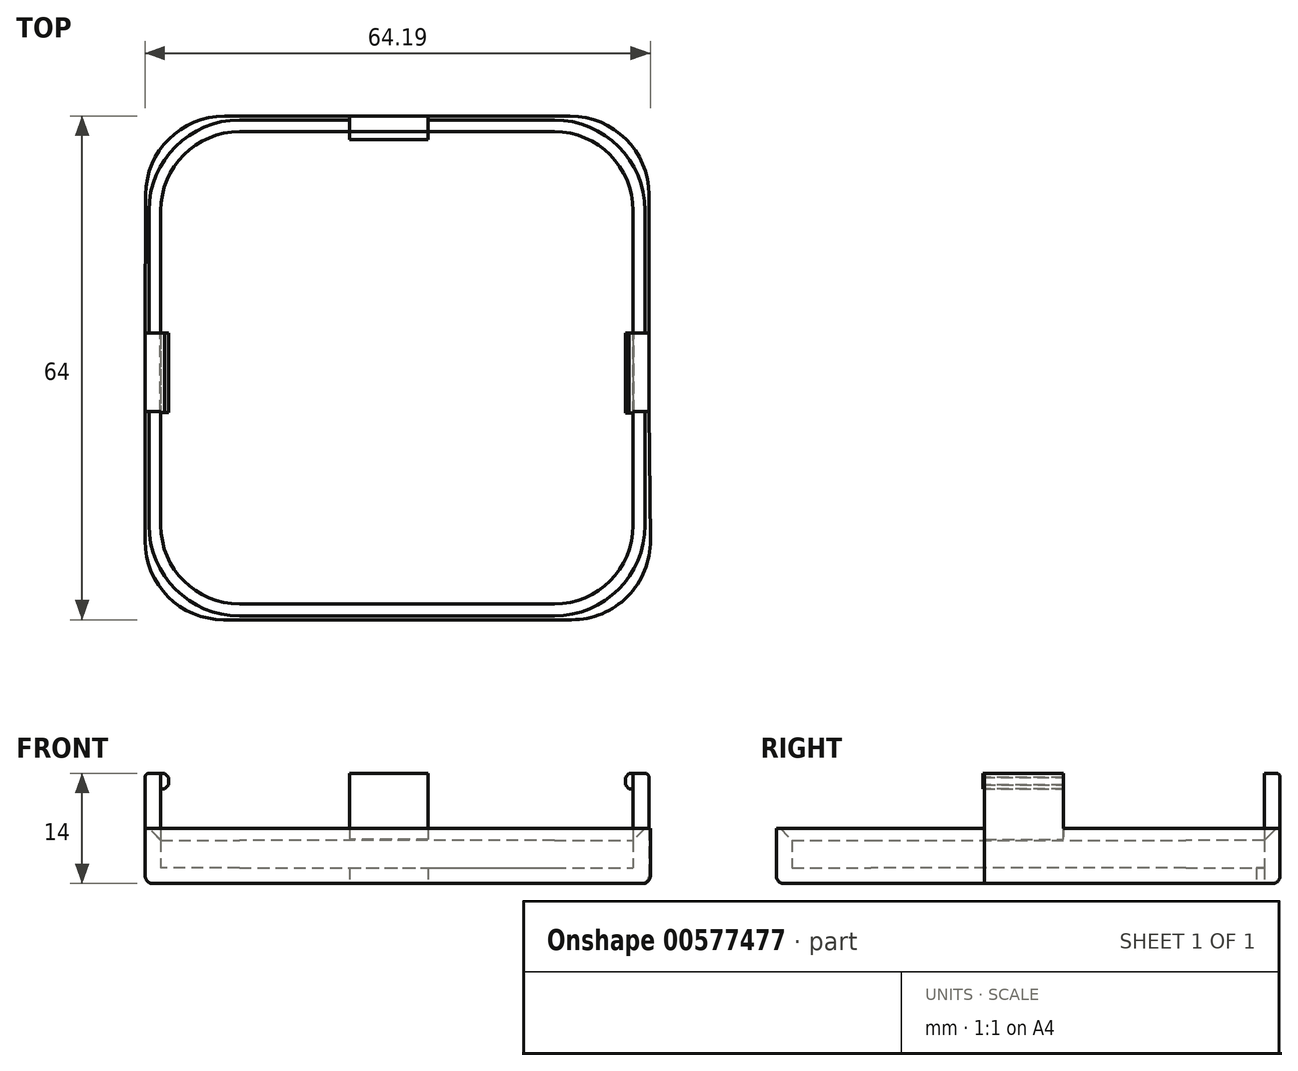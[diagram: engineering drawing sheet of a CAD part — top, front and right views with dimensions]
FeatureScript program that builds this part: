
annotation { "Feature Type Name" : "Feature", "Feature Type Description" : "" }
export const myFeature = defineFeature(function(context is Context, id is Id, definition is map)
    precondition{}
    {
        {
            var Q0;
            Q0=qCreatedBy(makeId("Top.planeOp"),FACE);
            var sketch = newSketch(context, id + "F0", { "sketchPlane" : qUnion([Q0])});
            skLineSegment(sketch, "E0.bottom", {"start": v(-28.96, 30.55) * mm, "end": v(31.04, 30.55) * mm});
            skLineSegment(sketch, "E0.top", {"start": v(-28.96, -29.45) * mm, "end": v(31.04, -29.45) * mm});
            skLineSegment(sketch, "E0.left", {"start": v(-28.96, 30.55) * mm, "end": v(-28.96, -29.45) * mm});
            skLineSegment(sketch, "E0.right", {"start": v(31.04, 30.55) * mm, "end": v(31.04, -29.45) * mm});
            skLineSegment(sketch, "E1.bottom", {"start": v(-5, 30.55) * mm, "end": v(5, 30.55) * mm});
            skLineSegment(sketch, "E1.top", {"start": v(-5, 32.55) * mm, "end": v(5, 32.55) * mm});
            skLineSegment(sketch, "E1.left", {"start": v(-5, 30.55) * mm, "end": v(-5, 32.55) * mm});
            skLineSegment(sketch, "E1.right", {"start": v(5, 30.55) * mm, "end": v(5, 32.55) * mm});
            skLineSegment(sketch, "E2.top", {"start": v(-5, 29.55) * mm, "end": v(5, 29.55) * mm});
            skLineSegment(sketch, "E2.left", {"start": v(-5, 30.55) * mm, "end": v(-5, 29.55) * mm});
            skLineSegment(sketch, "E2.right", {"start": v(5, 30.55) * mm, "end": v(5, 29.55) * mm});
            skLineSegment(sketch, "E3.bottom", {"start": v(31.04, 5) * mm, "end": v(33.04, 5) * mm});
            skLineSegment(sketch, "E3.top", {"start": v(31.04, -5) * mm, "end": v(33.04, -5) * mm});
            skLineSegment(sketch, "E3.left", {"start": v(31.04, 5) * mm, "end": v(31.04, -5) * mm});
            skLineSegment(sketch, "E3.right", {"start": v(33.04, 5) * mm, "end": v(33.04, -5) * mm});
            skLineSegment(sketch, "E4.bottom", {"start": v(31.04, 5) * mm, "end": v(30.04, 5) * mm});
            skLineSegment(sketch, "E4.top", {"start": v(31.04, -5.2) * mm, "end": v(30.04, -5.2) * mm});
            skLineSegment(sketch, "E4.left", {"start": v(31.04, 5) * mm, "end": v(31.04, -5.2) * mm});
            skLineSegment(sketch, "E4.right", {"start": v(30.04, 5) * mm, "end": v(30.04, -5.2) * mm});
            skLineSegment(sketch, "E5.bottom", {"start": v(-28.96, 5) * mm, "end": v(-30.96, 5) * mm});
            skLineSegment(sketch, "E5.top", {"start": v(-28.96, -5) * mm, "end": v(-30.96, -5) * mm});
            skLineSegment(sketch, "E5.left", {"start": v(-28.96, 5) * mm, "end": v(-28.96, -5) * mm});
            skLineSegment(sketch, "E5.right", {"start": v(-30.96, 5) * mm, "end": v(-30.96, -5) * mm});
            skLineSegment(sketch, "E6.bottom", {"start": v(-28.96, 5) * mm, "end": v(-27.96, 5) * mm});
            skLineSegment(sketch, "E6.top", {"start": v(-28.96, -5.13) * mm, "end": v(-27.96, -5.13) * mm});
            skLineSegment(sketch, "E6.left", {"start": v(-28.96, 5) * mm, "end": v(-28.96, -5.13) * mm});
            skLineSegment(sketch, "E6.right", {"start": v(-27.96, 5) * mm, "end": v(-27.96, -5.13) * mm});
            skLineSegment(sketch, "E7", {"start": v(-5, 32.55) * mm, "end": v(-30.83, 32.55) * mm});
            skLineSegment(sketch, "E8", {"start": v(-30.83, 32.55) * mm, "end": v(-30.96, 5) * mm});
            skLineSegment(sketch, "E9", {"start": v(-30.96, -5) * mm, "end": v(-30.96, -31.45) * mm});
            skLineSegment(sketch, "E10", {"start": v(-30.96, -31.45) * mm, "end": v(33.35, -31.45) * mm});
            skLineSegment(sketch, "E11", {"start": v(33.35, -31.45) * mm, "end": v(33.04, -5) * mm});
            skLineSegment(sketch, "E12", {"start": v(33.04, 5) * mm, "end": v(33.04, 32.55) * mm});
            skLineSegment(sketch, "E13", {"start": v(33.04, 32.55) * mm, "end": v(5, 32.55) * mm});
            skSolve(sketch);
        }
        {
            var Q0;
            {var subQ1=sQuery(id+"F0.wireOp",EDGE,"E1.right");Q0=makeQuery(id+"F0.imprint","IMPRINT",FACE,{"disambiguationData":[TD([[makeQuery(id+"F0.imprint","IMPRINT",EDGE,{"derivedFrom":subQ1}),-1.0]])]});}
            var Q1;
            Q1=makeQuery(id+"F0.imprint","IMPRINT",FACE,{"disambiguationData":[TD([[makeQuery(id+"F0.imprint","IMPRINT",EDGE,{"derivedFrom":sQuery(id+"F0.wireOp",EDGE,"E1.top")}),-1.0]])]});
            var Q2;
            {var subQ0=sQuery(id+"F0.wireOp",EDGE,"E3.bottom");Q2=makeQuery(id+"F0.imprint","IMPRINT",FACE,{"disambiguationData":[TD([[makeQuery(id+"F0.imprint","IMPRINT",EDGE,{"derivedFrom":subQ0}),-1.0]])]});}
            var Q3;
            {var subQ0=sQuery(id+"F0.wireOp",EDGE,"E5.bottom");Q3=makeQuery(id+"F0.imprint","IMPRINT",FACE,{"disambiguationData":[TD([[makeQuery(id+"F0.imprint","IMPRINT",EDGE,{"derivedFrom":subQ0}),1.0]])]});}
            var Q4;
            {var subQ2=sQuery(id+"F0.wireOp",EDGE,"E0.top");Q4=makeQuery(id+"F0.imprint","IMPRINT",FACE,{"disambiguationData":[TD([[makeQuery(id+"F0.imprint","IMPRINT",EDGE,{"derivedFrom":subQ2}),-1.0]])]});}
            var Q5;
            {var subQ4=sQuery(id+"F0.wireOp",EDGE,"E1.left");Q5=makeQuery(id+"F0.imprint","IMPRINT",FACE,{"disambiguationData":[TD([[makeQuery(id+"F0.imprint","IMPRINT",EDGE,{"derivedFrom":subQ4}),1.0]])]});}
            extrude(context, id + "F1", {"entities" : qUnion([Q0, Q1, Q2, Q3, Q4, Q5]), "depth" : 7 * mm, "offsetDistance" : 25 * mm});
        }
        {
            var Q0;
            {var subQ1=sQuery(id+"F0.wireOp",EDGE,"E0.top");Q0=makeQuery(id+"F0.imprint","IMPRINT",FACE,{"disambiguationData":[TD([[makeQuery(id+"F0.imprint","IMPRINT",EDGE,{"derivedFrom":subQ1}),1.0]])]});}
            var Q1;
            Q1=makeQuery(id+"F0.imprint","IMPRINT",FACE,{"disambiguationData":[TD([[makeQuery(id+"F0.imprint","IMPRINT",EDGE,{"derivedFrom":sQuery(id+"F0.wireOp",EDGE,"E1.bottom")}),-1.0]])]});
            var Q2;
            {var subQ4=sQuery(id+"F0.wireOp",EDGE,"E4.bottom");Q2=makeQuery(id+"F0.imprint","IMPRINT",FACE,{"disambiguationData":[TD([[makeQuery(id+"F0.imprint","IMPRINT",EDGE,{"derivedFrom":subQ4}),1.0]])]});}
            var Q3;
            {var subQ4=sQuery(id+"F0.wireOp",EDGE,"E6.bottom");Q3=makeQuery(id+"F0.imprint","IMPRINT",FACE,{"disambiguationData":[TD([[makeQuery(id+"F0.imprint","IMPRINT",EDGE,{"derivedFrom":subQ4}),-1.0]])]});}
            extrude(context, id + "F2", {"entities" : qUnion([Q0, Q1, Q2, Q3]), "operationType" : NewBodyOperationType.ADD, "depth" : 2 * mm, "offsetDistance" : 25 * mm});
        }
        {
            var Q0;
            Q0=makeQuery(id+"F0.imprint","IMPRINT",FACE,{"disambiguationData":[TD([[makeQuery(id+"F0.imprint","IMPRINT",EDGE,{"derivedFrom":sQuery(id+"F0.wireOp",EDGE,"E1.bottom")}),-1.0]])]});
            var Q1;
            {var subQ4=sQuery(id+"F0.wireOp",EDGE,"E6.bottom");Q1=makeQuery(id+"F0.imprint","IMPRINT",FACE,{"disambiguationData":[TD([[makeQuery(id+"F0.imprint","IMPRINT",EDGE,{"derivedFrom":subQ4}),-1.0]])]});}
            var Q2;
            {var subQ4=sQuery(id+"F0.wireOp",EDGE,"E4.bottom");Q2=makeQuery(id+"F0.imprint","IMPRINT",FACE,{"disambiguationData":[TD([[makeQuery(id+"F0.imprint","IMPRINT",EDGE,{"derivedFrom":subQ4}),1.0]])]});}
            var Q3;
            {var subQ0=sQuery(id+"F0.wireOp",EDGE,"E5.bottom");Q3=makeQuery(id+"F0.imprint","IMPRINT",FACE,{"disambiguationData":[TD([[makeQuery(id+"F0.imprint","IMPRINT",EDGE,{"derivedFrom":subQ0}),1.0]])]});}
            var Q4;
            Q4=makeQuery(id+"F0.imprint","IMPRINT",FACE,{"disambiguationData":[TD([[makeQuery(id+"F0.imprint","IMPRINT",EDGE,{"derivedFrom":sQuery(id+"F0.wireOp",EDGE,"E1.top")}),-1.0]])]});
            var Q5;
            {var subQ0=sQuery(id+"F0.wireOp",EDGE,"E3.bottom");Q5=makeQuery(id+"F0.imprint","IMPRINT",FACE,{"disambiguationData":[TD([[makeQuery(id+"F0.imprint","IMPRINT",EDGE,{"derivedFrom":subQ0}),-1.0]])]});}
            extrude(context, id + "F3", {"entities" : qUnion([Q0, Q1, Q2, Q3, Q4, Q5]), "operationType" : NewBodyOperationType.ADD, "depth" : 14 * mm, "offsetDistance" : 25 * mm, "hasSecondDirection" : true, "secondDirectionOppositeDirection" : false, "secondDirectionDepth" : 12 * mm});
        }
        {
            var Q0;
            Q0=makeQuery(id+"F1.opExtrude","SWEPT_EDGE",EDGE,{"disambiguationData":[OSD([sQuery(id+"F0.wireOp",EDGE,"E12"),sQuery(id+"F0.wireOp",EDGE,"E13")])]});
            var Q1;
            Q1=makeQuery(id+"F1.opExtrude","SWEPT_EDGE",EDGE,{"disambiguationData":[OSD([sQuery(id+"F0.wireOp",EDGE,"E7"),sQuery(id+"F0.wireOp",EDGE,"E8")])]});
            var Q2;
            Q2=makeQuery(id+"F1.opExtrude","SWEPT_EDGE",EDGE,{"disambiguationData":[OSD([sQuery(id+"F0.wireOp",EDGE,"E9"),sQuery(id+"F0.wireOp",EDGE,"E10")])]});
            var Q3;
            Q3=makeQuery(id+"F1.opExtrude","SWEPT_EDGE",EDGE,{"disambiguationData":[OSD([sQuery(id+"F0.wireOp",EDGE,"E10"),sQuery(id+"F0.wireOp",EDGE,"E11")])]});
            var Q4;
            Q4=makeQuery(id+"F1.opExtrude","SWEPT_EDGE",EDGE,{"disambiguationData":[OSD([sQuery(id+"F0.wireOp",EDGE,"E0.bottom"),sQuery(id+"F0.wireOp",EDGE,"E0.right")])]});
            var Q5;
            Q5=makeQuery(id+"F1.opExtrude","SWEPT_EDGE",EDGE,{"disambiguationData":[OSD([sQuery(id+"F0.wireOp",EDGE,"E0.bottom"),sQuery(id+"F0.wireOp",EDGE,"E0.left")])]});
            var Q6;
            Q6=makeQuery(id+"F1.opExtrude","SWEPT_EDGE",EDGE,{"disambiguationData":[OSD([sQuery(id+"F0.wireOp",EDGE,"E0.top"),sQuery(id+"F0.wireOp",EDGE,"E0.left")])]});
            var Q7;
            Q7=makeQuery(id+"F1.opExtrude","SWEPT_EDGE",EDGE,{"disambiguationData":[OSD([sQuery(id+"F0.wireOp",EDGE,"E0.top"),sQuery(id+"F0.wireOp",EDGE,"E0.right")])]});
            fillet(context, id + "F4", {"entities" : qUnion([Q0, Q1, Q2, Q3, Q4, Q5, Q6, Q7]), "radius" : 10 * mm, "tangentPropagation" : true, "allowEdgeOverflow" : false});
        }
        {
            var Q0;
            {var subQ0=sQuery(id+"F0.wireOp",EDGE,"E1.bottom");var subQ1=sQuery(id+"F0.wireOp",EDGE,"E6.left");var subQ2=sQuery(id+"F0.wireOp",EDGE,"E0.left");var subQ3=sQuery(id+"F0.wireOp",EDGE,"E0.bottom");var subQ4=makeQuery(id+"F1.opExtrude","CAP_FACE",FACE,{"disambiguationData":[OSD([subQ3,sQuery(id+"F0.wireOp",EDGE,"E0.top"),subQ2,sQuery(id+"F0.wireOp",EDGE,"E0.right"),sQuery(id+"F0.wireOp",EDGE,"E1.top"),subQ0,sQuery(id+"F0.wireOp",EDGE,"E3.right"),sQuery(id+"F0.wireOp",EDGE,"E4.left"),sQuery(id+"F0.wireOp",EDGE,"E5.right"),subQ1,sQuery(id+"F0.wireOp",EDGE,"E7"),sQuery(id+"F0.wireOp",EDGE,"E8"),sQuery(id+"F0.wireOp",EDGE,"E9"),sQuery(id+"F0.wireOp",EDGE,"E10"),sQuery(id+"F0.wireOp",EDGE,"E11"),sQuery(id+"F0.wireOp",EDGE,"E12"),sQuery(id+"F0.wireOp",EDGE,"E13")])],"isStart":false});var subQ5=makeQuery(id+"F1.opExtrude","SWEPT_FACE",FACE,{"disambiguationData":[OSD([subQ3,subQ0])]});Q0=makeQuery(id+"F3.boolean.opBoolean","SPLIT",EDGE,{"disambiguationData":[topologyDisambiguationEdgeConnected([subQ4,subQ5]),TD([makeQuery(id+"F3.opExtrude","SWEPT_FACE",FACE,{"disambiguationData":[OSD([sQuery(id+"F0.wireOp",EDGE,"E2.left")])]})])],"derivedFrom":makeQuery(id+"F1.opExtrude","CAP_EDGE",EDGE,{"disambiguationData":[OSD([subQ3,subQ0])],"isStart":false})});}
            var Q1;
            {var subQ0=sQuery(id+"F0.wireOp",EDGE,"E1.bottom");var subQ1=sQuery(id+"F0.wireOp",EDGE,"E4.left");var subQ2=sQuery(id+"F0.wireOp",EDGE,"E0.right");var subQ3=sQuery(id+"F0.wireOp",EDGE,"E0.bottom");var subQ4=makeQuery(id+"F1.opExtrude","CAP_FACE",FACE,{"disambiguationData":[OSD([subQ3,sQuery(id+"F0.wireOp",EDGE,"E0.top"),sQuery(id+"F0.wireOp",EDGE,"E0.left"),subQ2,sQuery(id+"F0.wireOp",EDGE,"E1.top"),subQ0,sQuery(id+"F0.wireOp",EDGE,"E3.right"),subQ1,sQuery(id+"F0.wireOp",EDGE,"E5.right"),sQuery(id+"F0.wireOp",EDGE,"E6.left"),sQuery(id+"F0.wireOp",EDGE,"E7"),sQuery(id+"F0.wireOp",EDGE,"E8"),sQuery(id+"F0.wireOp",EDGE,"E9"),sQuery(id+"F0.wireOp",EDGE,"E10"),sQuery(id+"F0.wireOp",EDGE,"E11"),sQuery(id+"F0.wireOp",EDGE,"E12"),sQuery(id+"F0.wireOp",EDGE,"E13")])],"isStart":false});var subQ5=makeQuery(id+"F1.opExtrude","SWEPT_FACE",FACE,{"disambiguationData":[OSD([subQ3,subQ0])]});Q1=makeQuery(id+"F3.boolean.opBoolean","SPLIT",EDGE,{"disambiguationData":[topologyDisambiguationEdgeConnected([subQ4,subQ5]),TD([makeQuery(id+"F3.opExtrude","SWEPT_FACE",FACE,{"disambiguationData":[OSD([sQuery(id+"F0.wireOp",EDGE,"E2.right")])]})])],"derivedFrom":makeQuery(id+"F1.opExtrude","CAP_EDGE",EDGE,{"disambiguationData":[OSD([subQ3,subQ0])],"isStart":false})});}
            var Q2;
            {var subQ0=sQuery(id+"F0.wireOp",EDGE,"E4.left");var subQ1=sQuery(id+"F0.wireOp",EDGE,"E0.right");var subQ2=makeQuery(id+"F1.opExtrude","SWEPT_FACE",FACE,{"disambiguationData":[OSD([subQ1,subQ0])]});var subQ3=sQuery(id+"F0.wireOp",EDGE,"E0.top");var subQ4=makeQuery(id+"F1.opExtrude","CAP_FACE",FACE,{"disambiguationData":[OSD([sQuery(id+"F0.wireOp",EDGE,"E0.bottom"),subQ3,sQuery(id+"F0.wireOp",EDGE,"E0.left"),subQ1,sQuery(id+"F0.wireOp",EDGE,"E1.top"),sQuery(id+"F0.wireOp",EDGE,"E1.bottom"),sQuery(id+"F0.wireOp",EDGE,"E3.right"),subQ0,sQuery(id+"F0.wireOp",EDGE,"E5.right"),sQuery(id+"F0.wireOp",EDGE,"E6.left"),sQuery(id+"F0.wireOp",EDGE,"E7"),sQuery(id+"F0.wireOp",EDGE,"E8"),sQuery(id+"F0.wireOp",EDGE,"E9"),sQuery(id+"F0.wireOp",EDGE,"E10"),sQuery(id+"F0.wireOp",EDGE,"E11"),sQuery(id+"F0.wireOp",EDGE,"E12"),sQuery(id+"F0.wireOp",EDGE,"E13")])],"isStart":false});Q2=makeQuery(id+"F3.boolean.opBoolean","SPLIT",EDGE,{"disambiguationData":[topologyDisambiguationEdgeConnected([subQ4,subQ2]),TD([makeQuery(id+"F1.opExtrude","SWEPT_FACE",FACE,{"disambiguationData":[OSD([subQ3])]})])],"derivedFrom":makeQuery(id+"F1.opExtrude","CAP_EDGE",EDGE,{"disambiguationData":[OSD([subQ1,subQ0])],"isStart":false})});}
            chamfer(context, id + "F5", {"entities" : qUnion([Q0, Q1, Q2]), "width" : 1.5 * mm, "tangentPropagation" : true});
        }
        {
            var Q0;
            Q0=makeQuery(id+"F0.imprint","IMPRINT",FACE,{"disambiguationData":[TD([[makeQuery(id+"F0.imprint","IMPRINT",EDGE,{"derivedFrom":sQuery(id+"F0.wireOp",EDGE,"E1.top")}),-1.0]])]});
            var Q1;
            {var subQ0=sQuery(id+"F0.wireOp",EDGE,"E3.bottom");Q1=makeQuery(id+"F0.imprint","IMPRINT",FACE,{"disambiguationData":[TD([[makeQuery(id+"F0.imprint","IMPRINT",EDGE,{"derivedFrom":subQ0}),-1.0]])]});}
            var Q2;
            {var subQ0=sQuery(id+"F0.wireOp",EDGE,"E5.bottom");Q2=makeQuery(id+"F0.imprint","IMPRINT",FACE,{"disambiguationData":[TD([[makeQuery(id+"F0.imprint","IMPRINT",EDGE,{"derivedFrom":subQ0}),1.0]])]});}
            extrude(context, id + "F6", {"entities" : qUnion([Q0, Q1, Q2]), "operationType" : NewBodyOperationType.ADD, "depth" : 12 * mm, "offsetDistance" : 25 * mm, "hasSecondDirection" : true, "secondDirectionOppositeDirection" : false, "secondDirectionDepth" : 5.6 * mm});
        }
        {
            var Q0;
            Q0=makeQuery(id+"F3.opExtrude","CAP_EDGE",EDGE,{"disambiguationData":[OSD([sQuery(id+"F0.wireOp",EDGE,"E2.top")])],"isStart":true});
            var Q1;
            Q1=makeQuery(id+"F3.opExtrude","CAP_EDGE",EDGE,{"disambiguationData":[OSD([sQuery(id+"F0.wireOp",EDGE,"E4.right")])],"isStart":true});
            var Q2;
            Q2=makeQuery(id+"F3.opExtrude","CAP_EDGE",EDGE,{"disambiguationData":[OSD([sQuery(id+"F0.wireOp",EDGE,"E6.right")])],"isStart":true});
            var Q3;
            Q3=makeQuery(id+"F3.opExtrude","CAP_EDGE",EDGE,{"disambiguationData":[OSD([sQuery(id+"F0.wireOp",EDGE,"E4.right")])],"isStart":false});
            var Q4;
            Q4=makeQuery(id+"F3.opExtrude","CAP_EDGE",EDGE,{"disambiguationData":[OSD([sQuery(id+"F0.wireOp",EDGE,"E6.right")])],"isStart":false});
            var Q5;
            Q5=makeQuery(id+"F3.opExtrude","CAP_EDGE",EDGE,{"disambiguationData":[OSD([sQuery(id+"F0.wireOp",EDGE,"E2.top")])],"isStart":false});
            chamfer(context, id + "F7", {"entities" : qUnion([Q0, Q1, Q2, Q3, Q4, Q5]), "width" : .5 * mm, "tangentPropagation" : true});
        }
        {
            var Q0;
            Q0=makeQuery(id+"F1.opExtrude","CAP_EDGE",EDGE,{"disambiguationData":[OSD([sQuery(id+"F0.wireOp",EDGE,"E8")])],"isStart":true});
            var Q1;
            Q1=makeQuery(id+"F1.opExtrude","CAP_EDGE",EDGE,{"disambiguationData":[OSD([sQuery(id+"F0.wireOp",EDGE,"E10")])],"isStart":true});
            fillet(context, id + "F8", {"entities" : qUnion([Q0, Q1]), "radius" : 1 * mm, "tangentPropagation" : true, "allowEdgeOverflow" : false});
        }
        {
            var Q0;
            Q0=makeQuery(id+"F3.opExtrude","CAP_EDGE",EDGE,{"disambiguationData":[OSD([sQuery(id+"F0.wireOp",EDGE,"E5.right")])],"isStart":false});
            var Q1;
            Q1=makeQuery(id+"F3.opExtrude","CAP_EDGE",EDGE,{"disambiguationData":[OSD([sQuery(id+"F0.wireOp",EDGE,"E3.right")])],"isStart":false});
            var Q2;
            Q2=makeQuery(id+"F3.opExtrude","CAP_EDGE",EDGE,{"disambiguationData":[OSD([sQuery(id+"F0.wireOp",EDGE,"E1.top")])],"isStart":false});
            fillet(context, id + "F9", {"entities" : qUnion([Q0, Q1, Q2]), "radius" : .5 * mm, "tangentPropagation" : true, "allowEdgeOverflow" : false});
        }
    });
